# Revit family: Univers-IP41-leer-Aufputz-AT-de
name_source: partatom
category: Electrical Equipment
units: mm (PartAtom-declared; Revit-internal decimal feet)

## family parameters
Cut with Voids When Loaded = No
Host = Face
Panel Configuration = Two Columns, Circuits Across
Part Type = Panelboard
Room Calculation Point = No
Round Connector Dimension = Use Diameter
Shared = No

## types (3) — shared parameters
EF000003 - Montageart = EV000384 - Aufputz
EF000007 - Farbe = EV000202 - weiß
EF000116 - RAL-Nummer = 9010
EF000118 - Mit Montageplatte = No
EF000218 - Einbautiefe = 84 mm  [stored 0.275591 ft]
EF000339 - Art der Abdeckung = EV004216 - Tür
EF001062 - EMV-Ausführung = No
EF001088 - Anbaumöglichkeit = No
EF001131 - Innentiefe = 84 mm  [stored 0.275591 ft]
EF001134 - DIN-Schiene = No
EF001596 - Werkstoff des Gehäuses = EV000154 - sonstige
EF005474 - Schutzart (IP) = EV006416 - IP41
EF006244 - Transparenter Deckel/Tür = No
EF006306 - Mit Schloss = No
EF009212 - Ausführung Deckel = EV000116 - geschlossen
EF015776 - Erdungsklemmenblock = No
EF015777 - Neutralleiterklemmenblock = No
EF015941 - Signaldurchlassende Tür = No
HG000002 - Mit tür = Yes
HG000003 - Bereich = Univers
HG000005 - Dicke = 3 mm  [stored 0.00984252 ft]
HG000006 - Unterputz = No
HG000009 - Doppelflügeligen Tür = No
HG000010 - Asymmetrische Türen = No
HG000011 - Leere Reihen von unten = No
Manufacturer = Hager
Type Comments = Univers
zero-valued in all types: Default Elevation, EF000266 - Anzahl der Reihen, EF000332 - Einbauhöhe, EF002950 - Breite in Teilungseinheiten, HG000001 - Anzahl der Spalten, HG000007 - Anzahl der leeren Spalten, HG000008 - Anzahl der leeren Reihen

## per-type parameters (varying)
| type | EF000008 - Breite | EF000040 - Höhe | EF000049 - Tiefe | EF000846 - Einbaubreite | EF004462 - Art der Schließung | HG000004 - Herstellerreferenz | Model |
| Aufputz IP41 B350 H350 T128 0 Teilungseinheiten - FB2008LN | 350 mm | 350 mm | 128 mm | 200 mm  [stored 0.656168 ft] | EV000154 - sonstige | FB2008LN | FB2008LN |
| Aufputz IP41 B450 H450 T128 0 Teilungseinheiten - FB3008LN | 450 mm  [stored 1.47638 ft] | 450 mm  [stored 1.47638 ft] | 128 mm | 300 mm | EV000154 - sonstige | FB3008LN | FB3008LN |
| Aufputz IP41 B540 H450 T148 0 Teilungseinheiten - FB3008SN | 540 mm  [stored 1.77165 ft] | 450 mm  [stored 1.47638 ft] | 148 mm  [stored 0.485564 ft] | 300 mm | 0 | FB3008SN | FB3008SN |

note: [stored X ft] marks values corroborated as IEEE doubles in the binary element streams (Revit-internal decimal feet)

## geometry (parser evidence)
native form markers: Sweep x12
no freeform markers — native parametric forms only
